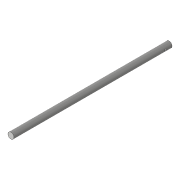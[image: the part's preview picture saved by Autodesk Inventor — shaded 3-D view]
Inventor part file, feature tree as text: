
AUTODESK INVENTOR PART (.ipt)
format: ipt  version: 2019 (Build 230136000, 136)  size: 92,160 bytes
history: native  units: in
note: dims shown in document units (in); Inventor stores cm internally (conversion verified against a paired STEP export)
features: extrude x2, sketch x2, thread x1
ambient origin geometry x8: Origin, YZ Plane, XZ Plane, XY Plane, X Axis, Y Axis, Z Axis, Center Point
bodies: Solid1 (feature_tree)
feature tree (5):
  extrude  "Extrusion1"  Depth=9.252in TaperAngle=0.0deg
  extrude  "Extrusion2"  Depth=0.3937in
  thread  "Thread1"  [1 undecoded]
  sketch  "Sketch1"  dims[d0=0.3543in d1=9.252in d2=0.0in]
  sketch  "Sketch2"  dims[d3=0.0394in d4=0.3937in d5=0.3937in d6=0.0787in d7=0.0in d8=0.0in d9=0.3937in d10=0.0in]
note: 1 required parameter value undecoded (feature->parameter linkage not recoverable at this tier; creation-order binding heuristic only, values carry confidence <= 0.55)
